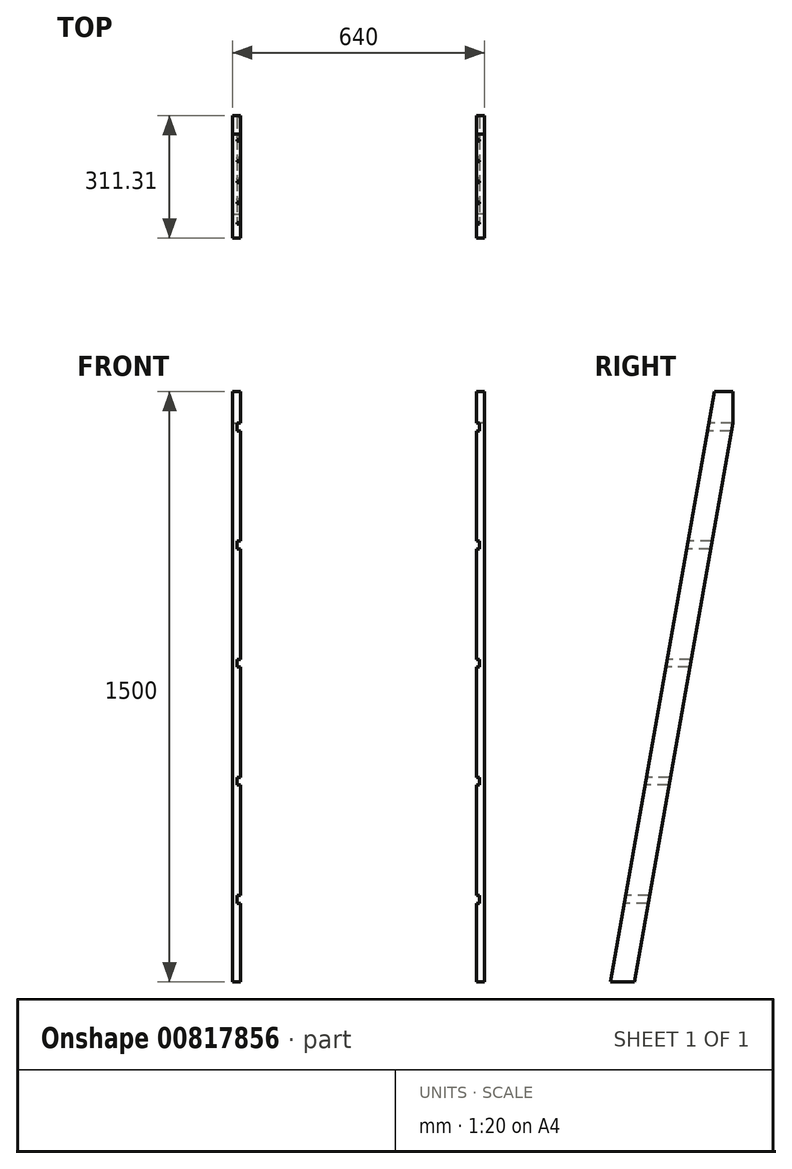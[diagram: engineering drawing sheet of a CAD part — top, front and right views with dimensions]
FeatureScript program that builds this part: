
annotation { "Feature Type Name" : "Feature", "Feature Type Description" : "" }
export const myFeature = defineFeature(function(context is Context, id is Id, definition is map)
    precondition{}
    {
        {
            var Q0;
            Q0=qCreatedBy(makeId("Right.planeOp"),FACE);
            var sketch = newSketch(context, id + "F0", { "sketchPlane" : qUnion([Q0])});
            skLineSegment(sketch, "E0", {"start": v(0, 0) * mm, "end": v(60.93, 0) * mm});
            skLineSegment(sketch, "E1", {"start": v(60.93, 0) * mm, "end": v(325.42, 1500) * mm});
            skLineSegment(sketch, "E2", {"start": v(325.42, 1500) * mm, "end": v(264.5, 1500) * mm});
            skLineSegment(sketch, "E3", {"start": v(264.5, 1500) * mm, "end": v(0, 0) * mm});
            skSolve(sketch);
        }
        {
            var Q0;
            Q0=makeQuery(id+"F0.imprint","IMPRINT",FACE,{"disambiguationData":[TD([[makeQuery(id+"F0.imprint","IMPRINT",EDGE,{"derivedFrom":sQuery(id+"F0.wireOp",EDGE,"E0")}),1.0]])]});
            extrude(context, id + "F1", {"entities" : qUnion([Q0]), "depth" : 20 * mm, "offsetDistance" : 25 * mm});
        }
        {
            var Q0;
            Q0=makeQuery(id+"F1.opExtrude","CAP_FACE",FACE,{"disambiguationData":[OSD([sQuery(id+"F0.wireOp",EDGE,"E0"),sQuery(id+"F0.wireOp",EDGE,"E1"),sQuery(id+"F0.wireOp",EDGE,"E2"),sQuery(id+"F0.wireOp",EDGE,"E3")])],"isStart":true});
            var sketch = newSketch(context, id + "F2", { "sketchPlane" : qUnion([Q0])});
            skLineSegment(sketch, "E4.0", {"start": v(-250.38, 1420) * mm, "end": v(-246.86, 1400) * mm});
            skLineSegment(sketch, "E5.0", {"start": v(-96.2, 200) * mm, "end": v(-99.72, 220) * mm});
            skLineSegment(sketch, "E6", {"start": v(-96.2, 200) * mm, "end": v(-35.27, 200) * mm});
            skLineSegment(sketch, "E7", {"start": v(-99.72, 220) * mm, "end": v(-38.8, 220) * mm});
            skLineSegment(sketch, "E8", {"start": v(-149.09, 500) * mm, "end": v(-88.16, 500) * mm});
            skLineSegment(sketch, "E9", {"start": v(-152.62, 520) * mm, "end": v(-91.7, 520) * mm});
            skLineSegment(sketch, "E10", {"start": v(-201.99, 800) * mm, "end": v(-141.06, 800) * mm});
            skLineSegment(sketch, "E11", {"start": v(-205.51, 820) * mm, "end": v(-144.59, 820) * mm});
            skLineSegment(sketch, "E12", {"start": v(-254.89, 1100) * mm, "end": v(-193.96, 1100) * mm});
            skLineSegment(sketch, "E13", {"start": v(-258.41, 1120) * mm, "end": v(-197.49, 1120) * mm});
            skLineSegment(sketch, "E14", {"start": v(-307.78, 1400) * mm, "end": v(-246.86, 1400) * mm});
            skLineSegment(sketch, "E15", {"start": v(-311.3, 1420) * mm, "end": v(-250.38, 1420) * mm});
            skPoint(sketch, "E16.orphan", {"position": v(-325.42, 1500) * mm});
            skPoint(sketch, "E17.orphan", {"position": v(-264.5, 1500) * mm});
            skLineSegment(sketch, "E18.trimOffspring", {"start": v(-307.78, 1400) * mm, "end": v(-311.3, 1420) * mm});
            skLineSegment(sketch, "E19.trimOffspring", {"start": v(-197.49, 1120) * mm, "end": v(-193.96, 1100) * mm});
            skLineSegment(sketch, "E20.trimOffspring", {"start": v(-254.89, 1100) * mm, "end": v(-258.41, 1120) * mm});
            skLineSegment(sketch, "E21.trimOffspring", {"start": v(-144.59, 820) * mm, "end": v(-141.06, 800) * mm});
            skLineSegment(sketch, "E22.trimOffspring", {"start": v(-201.99, 800) * mm, "end": v(-205.51, 820) * mm});
            skLineSegment(sketch, "E23.trimOffspring", {"start": v(-91.7, 520) * mm, "end": v(-88.16, 500) * mm});
            skLineSegment(sketch, "E24.trimOffspring", {"start": v(-149.09, 500) * mm, "end": v(-152.62, 520) * mm});
            skLineSegment(sketch, "E25.trimOffspring", {"start": v(-38.8, 220) * mm, "end": v(-35.27, 200) * mm});
            skPoint(sketch, "E26.orphan", {"position": v(-60.93, 0) * mm});
            skPoint(sketch, "E27.orphan", {"position": v(0, 0) * mm});
            skSolve(sketch);
        }
        {
            var Q0;
            Q0 = qSketchRegion(id + "F2", true);
            extrude(context, id + "F3", {"entities" : qUnion([Q0]), "operationType" : NewBodyOperationType.REMOVE, "oppositeDirection" : true, "depth" : 8 * mm, "offsetDistance" : 25 * mm});
        }
        {
            var Q0;
            {var subQ0=sQuery(id+"F0.wireOp",EDGE,"E1");var subQ1=sQuery(id+"F0.wireOp",EDGE,"E2");var subQ2=sQuery(id+"F0.wireOp",EDGE,"E3");Q0=makeQuery(id+"F3.boolean.opBoolean","SPLIT",FACE,{"disambiguationData":[TD([makeQuery(id+"F1.opExtrude","SWEPT_FACE",FACE,{"disambiguationData":[OSD([subQ1])]})])],"derivedFrom":makeQuery(id+"F1.opExtrude","CAP_FACE",FACE,{"disambiguationData":[OSD([sQuery(id+"F0.wireOp",EDGE,"E0"),subQ0,subQ1,subQ2])],"isStart":true})});}
            var sketch = newSketch(context, id + "F4", { "sketchPlane" : qUnion([Q0])});
            skLineSegment(sketch, "E28.0", {"start": v(-311.3, 1420) * mm, "end": v(-325.42, 1500) * mm});
            skLineSegment(sketch, "E29.0", {"start": v(-325.42, 1500) * mm, "end": v(-311.3, 1500) * mm});
            skLineSegment(sketch, "E30", {"start": v(-311.3, 1420) * mm, "end": v(-311.3, 1500) * mm});
            skPoint(sketch, "E31.orphan", {"position": v(-264.5, 1500) * mm});
            skSolve(sketch);
        }
        {
            var Q0;
            Q0 = qSketchRegion(id + "F4", true);
            extrude(context, id + "F5", {"entities" : qUnion([Q0]), "operationType" : NewBodyOperationType.REMOVE, "endBound" : BoundingType.THROUGH_ALL, "oppositeDirection" : true, "depth" : 25 * mm, "offsetDistance" : 25 * mm});
        }
        {
            var Q0;
            Q0=qCreatedBy(makeId("Right.planeOp"),FACE);
            cPlane(context, id + "F6", {"entities" : qUnion([Q0]), "cplaneType" : CPlaneType.OFFSET, "offset" : 300 * mm, "oppositeDirection" : true, "width" : 150 * mm, "height" : 150 * mm});
        }
        {
            var Q0;
            Q0=makeQuery(id+"F1.opExtrude","SWEPT_BODY",BODY,{"disambiguationData":[OSD([sQuery(id+"F0.wireOp",EDGE,"E0"),sQuery(id+"F0.wireOp",EDGE,"E1"),sQuery(id+"F0.wireOp",EDGE,"E2"),sQuery(id+"F0.wireOp",EDGE,"E3")])]});
            var Q1;
            Q1=qCreatedBy(id+"F6.planeOp",FACE);
            mirror(context, id + "F7", {"entities" : qUnion([Q0]), "mirrorPlane" : qUnion([Q1])});
        }
    });
